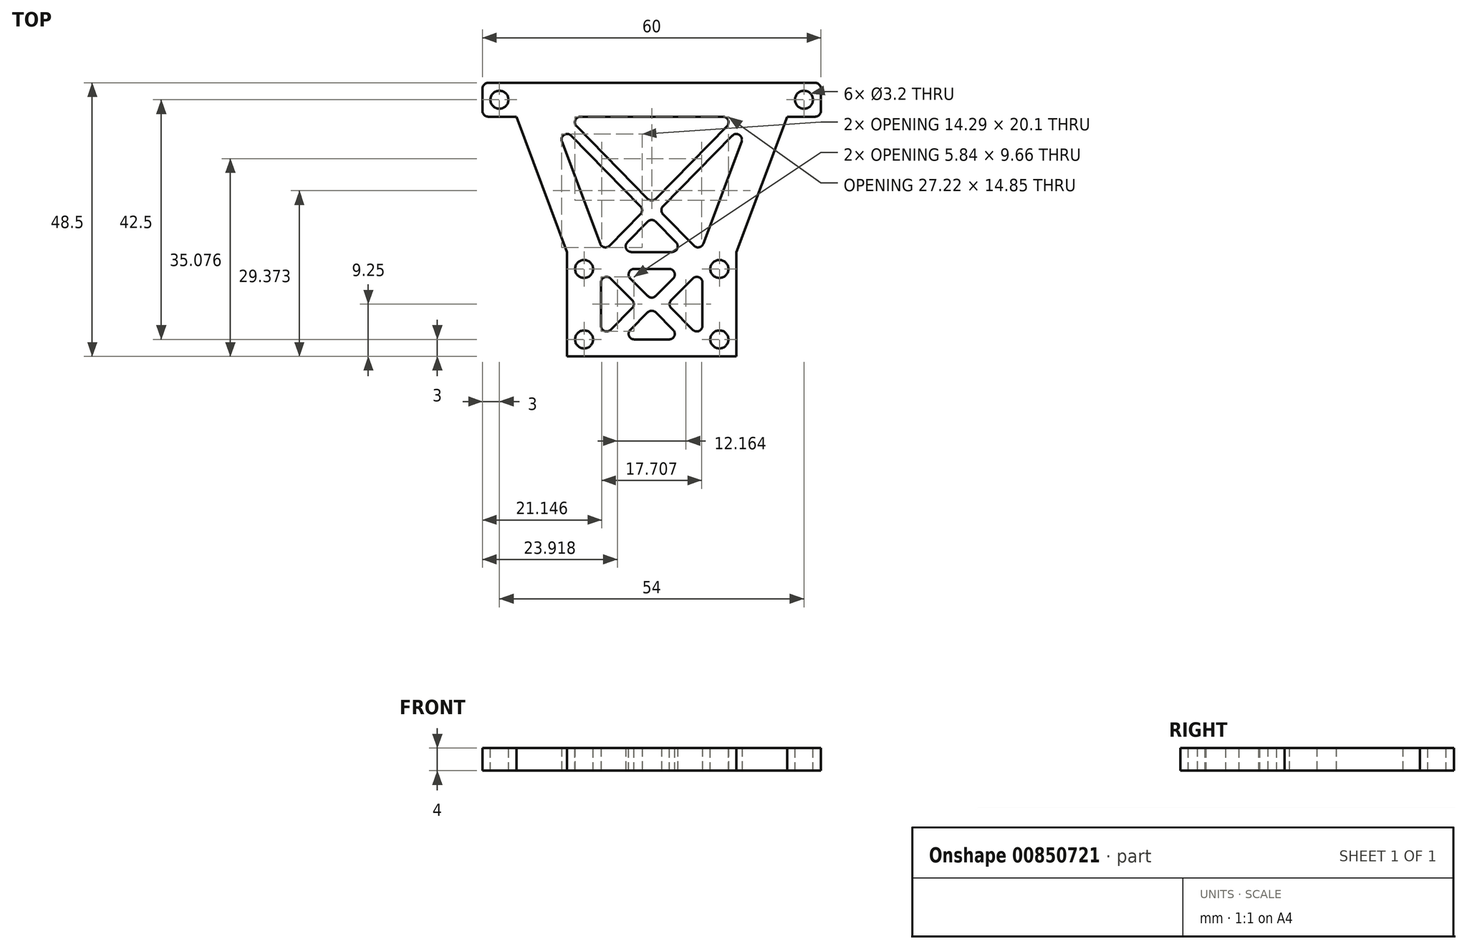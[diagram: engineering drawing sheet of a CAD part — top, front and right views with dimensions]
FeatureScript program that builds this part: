
annotation { "Feature Type Name" : "Feature", "Feature Type Description" : "" }
export const myFeature = defineFeature(function(context is Context, id is Id, definition is map)
    precondition{}
    {
        {
            var Q0;
            Q0=qCreatedBy(makeId("Top.planeOp"),FACE);
            var sketch = newSketch(context, id + "F0", { "sketchPlane" : qUnion([Q0])});
            skLineSegment(sketch, "E0", {"start": v(-15, -9.25) * mm, "end": v(15, -9.25) * mm});
            skLineSegment(sketch, "E1", {"start": v(15, -9.25) * mm, "end": v(15, 9.25) * mm});
            skLineSegment(sketch, "E2", {"start": v(15, 9.25) * mm, "end": v(24, 33.25) * mm});
            skLineSegment(sketch, "E3", {"start": v(24, 33.25) * mm, "end": v(30, 33.25) * mm});
            skLineSegment(sketch, "E4", {"start": v(30, 33.25) * mm, "end": v(30, 39.25) * mm});
            skLineSegment(sketch, "E5", {"start": v(30, 39.25) * mm, "end": v(-30, 39.25) * mm});
            skLineSegment(sketch, "E6", {"start": v(-30, 39.25) * mm, "end": v(-30, 33.25) * mm});
            skLineSegment(sketch, "E7", {"start": v(-30, 33.25) * mm, "end": v(-24, 33.25) * mm});
            skLineSegment(sketch, "E8", {"start": v(-24, 33.25) * mm, "end": v(-15, 9.25) * mm});
            skLineSegment(sketch, "E9", {"start": v(-15, 9.25) * mm, "end": v(-15, -9.25) * mm});
            skLineSegment(sketch, "E10", {"start": v(-15, 9.25) * mm, "end": v(15, 9.25) * mm, "construction": true});
            skSolve(sketch);
        }
        {
            var Q0;
            Q0 = qSketchRegion(id + "F0", true);
            extrude(context, id + "F1", {"entities" : qUnion([Q0]), "depth" : 4 * mm, "offsetDistance" : 25 * mm});
        }
        {
            var Q0;
            Q0=makeQuery(id+"F1.opExtrude","CAP_FACE",FACE,{"disambiguationData":[OSD([sQuery(id+"F0.wireOp",EDGE,"E0"),sQuery(id+"F0.wireOp",EDGE,"E1"),sQuery(id+"F0.wireOp",EDGE,"E2"),sQuery(id+"F0.wireOp",EDGE,"E3"),sQuery(id+"F0.wireOp",EDGE,"E4"),sQuery(id+"F0.wireOp",EDGE,"E5"),sQuery(id+"F0.wireOp",EDGE,"E6"),sQuery(id+"F0.wireOp",EDGE,"E7"),sQuery(id+"F0.wireOp",EDGE,"E8"),sQuery(id+"F0.wireOp",EDGE,"E9")])],"isStart":false});
            var sketch = newSketch(context, id + "F2", { "sketchPlane" : qUnion([Q0])});
            skLineSegment(sketch, "E11.bottom", {"start": v(-12, -6.25) * mm, "end": v(12, -6.25) * mm, "construction": true});
            skLineSegment(sketch, "E11.top", {"start": v(-12, 6.25) * mm, "end": v(12, 6.25) * mm, "construction": true});
            skLineSegment(sketch, "E11.left", {"start": v(-12, -6.25) * mm, "end": v(-12, 6.25) * mm, "construction": true});
            skLineSegment(sketch, "E11.right", {"start": v(12, -6.25) * mm, "end": v(12, 6.25) * mm, "construction": true});
            skLineSegment(sketch, "E12", {"start": v(-15, 9.25) * mm, "end": v(15, 9.25) * mm, "construction": true});
            skLineSegment(sketch, "E13", {"start": v(-12, -6.25) * mm, "end": v(-15, -6.25) * mm, "construction": true});
            skLineSegment(sketch, "E14", {"start": v(-12, -6.25) * mm, "end": v(-12, -9.25) * mm, "construction": true});
            skLineSegment(sketch, "E15", {"start": v(12, 6.25) * mm, "end": v(12, 9.25) * mm, "construction": true});
            skLineSegment(sketch, "E16", {"start": v(12, 6.25) * mm, "end": v(15, 6.25) * mm, "construction": true});
            skCircle(sketch, "E17", {"center": v(-12, 6.25) * mm, "radius": 1.6 * mm});
            skCircle(sketch, "E18", {"center": v(12, 6.25) * mm, "radius": 1.6 * mm});
            skCircle(sketch, "E19", {"center": v(-12, -6.25) * mm, "radius": 1.6 * mm});
            skCircle(sketch, "E20", {"center": v(12, -6.25) * mm, "radius": 1.6 * mm});
            skLineSegment(sketch, "E21", {"start": v(-24, 33.25) * mm, "end": v(-30, 39.25) * mm, "construction": true});
            skLineSegment(sketch, "E22", {"start": v(24, 33.25) * mm, "end": v(30, 39.25) * mm, "construction": true});
            skCircle(sketch, "E23", {"center": v(27, 36.25) * mm, "radius": 1.6 * mm});
            skCircle(sketch, "E24", {"center": v(-27, 36.25) * mm, "radius": 1.6 * mm});
            skSolve(sketch);
        }
        {
            var Q0;
            Q0 = qSketchRegion(id + "F2", true);
            extrude(context, id + "F3", {"entities" : qUnion([Q0]), "operationType" : NewBodyOperationType.REMOVE, "endBound" : BoundingType.UP_TO_NEXT, "oppositeDirection" : true, "depth" : 25 * mm, "offsetDistance" : 25 * mm});
        }
        {
            var Q0;
            Q0=makeQuery(id+"F1.opExtrude","CAP_FACE",FACE,{"disambiguationData":[OSD([sQuery(id+"F0.wireOp",EDGE,"E0"),sQuery(id+"F0.wireOp",EDGE,"E1"),sQuery(id+"F0.wireOp",EDGE,"E2"),sQuery(id+"F0.wireOp",EDGE,"E3"),sQuery(id+"F0.wireOp",EDGE,"E4"),sQuery(id+"F0.wireOp",EDGE,"E5"),sQuery(id+"F0.wireOp",EDGE,"E6"),sQuery(id+"F0.wireOp",EDGE,"E7"),sQuery(id+"F0.wireOp",EDGE,"E8"),sQuery(id+"F0.wireOp",EDGE,"E9")])],"isStart":false});
            var sketch = newSketch(context, id + "F4", { "sketchPlane" : qUnion([Q0])});
            skLineSegment(sketch, "E25", {"start": v(-17.6, 33.25) * mm, "end": v(-8.6, 9.25) * mm});
            skLineSegment(sketch, "E26", {"start": v(-8.6, 9.25) * mm, "end": v(-1.3, 16.67) * mm});
            skLineSegment(sketch, "E27", {"start": v(-1.3, 16.67) * mm, "end": v(-17.6, 33.25) * mm});
            skLineSegment(sketch, "E28", {"start": v(17.6, 33.25) * mm, "end": v(8.6, 9.25) * mm});
            skLineSegment(sketch, "E29", {"start": v(8.6, 9.25) * mm, "end": v(1.3, 16.67) * mm});
            skLineSegment(sketch, "E30", {"start": v(1.3, 16.67) * mm, "end": v(17.6, 33.25) * mm});
            skLineSegment(sketch, "E31", {"start": v(-15, 33.25) * mm, "end": v(15, 33.25) * mm});
            skLineSegment(sketch, "E32", {"start": v(15, 33.25) * mm, "end": v(0, 17.98) * mm});
            skLineSegment(sketch, "E33", {"start": v(0, 17.98) * mm, "end": v(-15, 33.25) * mm});
            skLineSegment(sketch, "E34", {"start": v(-6, 9.25) * mm, "end": v(6, 9.25) * mm});
            skLineSegment(sketch, "E35", {"start": v(6, 9.25) * mm, "end": v(0, 15.36) * mm});
            skLineSegment(sketch, "E36", {"start": v(0, 15.36) * mm, "end": v(-6, 9.25) * mm});
            skLineSegment(sketch, "E37", {"start": v(-24, 33.25) * mm, "end": v(24, 33.25) * mm, "construction": true});
            skLineSegment(sketch, "E38", {"start": v(-15, 9.25) * mm, "end": v(15, 9.25) * mm, "construction": true});
            skLineSegment(sketch, "E39", {"start": v(-1.3, 16.67) * mm, "end": v(0, 15.36) * mm, "construction": true});
            skLineSegment(sketch, "E40", {"start": v(0, 15.36) * mm, "end": v(1.3, 16.67) * mm, "construction": true});
            skLineSegment(sketch, "E41", {"start": v(1.3, 16.67) * mm, "end": v(0, 17.98) * mm, "construction": true});
            skLineSegment(sketch, "E42", {"start": v(0, 17.98) * mm, "end": v(-1.3, 16.67) * mm, "construction": true});
            skLineSegment(sketch, "E43", {"start": v(-12.62, 19.99) * mm, "end": v(-18.24, 17.88) * mm, "construction": true});
            skSolve(sketch);
        }
        {
            var Q0;
            Q0 = qSketchRegion(id + "F4", true);
            extrude(context, id + "F5", {"entities" : qUnion([Q0]), "operationType" : NewBodyOperationType.REMOVE, "endBound" : BoundingType.UP_TO_NEXT, "oppositeDirection" : true, "depth" : 25 * mm, "offsetDistance" : 25 * mm});
        }
        {
            var Q0;
            Q0=makeQuery(id+"F5.boolean.opBoolean","COPY",EDGE,{"derivedFrom":makeQuery(id+"F5.opExtrude","SWEPT_EDGE",EDGE,{"disambiguationData":[OSD([sQuery(id+"F4.wireOp",EDGE,"E28"),sQuery(id+"F4.wireOp",EDGE,"E30")])]})});
            var Q1;
            Q1=makeQuery(id+"F5.boolean.opBoolean","COPY",EDGE,{"derivedFrom":makeQuery(id+"F5.opExtrude","SWEPT_EDGE",EDGE,{"disambiguationData":[OSD([sQuery(id+"F4.wireOp",EDGE,"E31"),sQuery(id+"F4.wireOp",EDGE,"E32")])]})});
            var Q2;
            Q2=makeQuery(id+"F5.boolean.opBoolean","COPY",EDGE,{"derivedFrom":makeQuery(id+"F5.opExtrude","SWEPT_EDGE",EDGE,{"disambiguationData":[OSD([sQuery(id+"F4.wireOp",EDGE,"E31"),sQuery(id+"F4.wireOp",EDGE,"E33")])]})});
            var Q3;
            Q3=makeQuery(id+"F5.boolean.opBoolean","COPY",EDGE,{"derivedFrom":makeQuery(id+"F5.opExtrude","SWEPT_EDGE",EDGE,{"disambiguationData":[OSD([sQuery(id+"F4.wireOp",EDGE,"E25"),sQuery(id+"F4.wireOp",EDGE,"E27")])]})});
            var Q4;
            Q4=makeQuery(id+"F5.boolean.opBoolean","COPY",EDGE,{"derivedFrom":makeQuery(id+"F5.opExtrude","SWEPT_EDGE",EDGE,{"disambiguationData":[OSD([sQuery(id+"F4.wireOp",EDGE,"E32"),sQuery(id+"F4.wireOp",EDGE,"E33")])]})});
            var Q5;
            Q5=makeQuery(id+"F5.boolean.opBoolean","COPY",EDGE,{"derivedFrom":makeQuery(id+"F5.opExtrude","SWEPT_EDGE",EDGE,{"disambiguationData":[OSD([sQuery(id+"F4.wireOp",EDGE,"E28"),sQuery(id+"F4.wireOp",EDGE,"E29")])]})});
            var Q6;
            Q6=makeQuery(id+"F5.boolean.opBoolean","COPY",EDGE,{"derivedFrom":makeQuery(id+"F5.opExtrude","SWEPT_EDGE",EDGE,{"disambiguationData":[OSD([sQuery(id+"F4.wireOp",EDGE,"E25"),sQuery(id+"F4.wireOp",EDGE,"E26")])]})});
            var Q7;
            Q7=makeQuery(id+"F5.boolean.opBoolean","COPY",EDGE,{"derivedFrom":makeQuery(id+"F5.opExtrude","SWEPT_EDGE",EDGE,{"disambiguationData":[OSD([sQuery(id+"F4.wireOp",EDGE,"E34"),sQuery(id+"F4.wireOp",EDGE,"E36")])]})});
            var Q8;
            Q8=makeQuery(id+"F5.boolean.opBoolean","COPY",EDGE,{"derivedFrom":makeQuery(id+"F5.opExtrude","SWEPT_EDGE",EDGE,{"disambiguationData":[OSD([sQuery(id+"F4.wireOp",EDGE,"E34"),sQuery(id+"F4.wireOp",EDGE,"E35")])]})});
            var Q9;
            Q9=makeQuery(id+"F5.boolean.opBoolean","COPY",EDGE,{"derivedFrom":makeQuery(id+"F5.opExtrude","SWEPT_EDGE",EDGE,{"disambiguationData":[OSD([sQuery(id+"F4.wireOp",EDGE,"E35"),sQuery(id+"F4.wireOp",EDGE,"E36")])]})});
            var Q10;
            Q10=makeQuery(id+"F5.boolean.opBoolean","COPY",EDGE,{"derivedFrom":makeQuery(id+"F5.opExtrude","SWEPT_EDGE",EDGE,{"disambiguationData":[OSD([sQuery(id+"F4.wireOp",EDGE,"E26"),sQuery(id+"F4.wireOp",EDGE,"E27")])]})});
            var Q11;
            Q11=makeQuery(id+"F5.boolean.opBoolean","COPY",EDGE,{"derivedFrom":makeQuery(id+"F5.opExtrude","SWEPT_EDGE",EDGE,{"disambiguationData":[OSD([sQuery(id+"F4.wireOp",EDGE,"E29"),sQuery(id+"F4.wireOp",EDGE,"E30")])]})});
            fillet(context, id + "F6", {"entities" : qUnion([Q0, Q1, Q2, Q3, Q4, Q5, Q6, Q7, Q8, Q9, Q10, Q11]), "radius" : 1 * mm, "tangentPropagation" : true, "allowEdgeOverflow" : false});
        }
        {
            var Q0;
            Q0=makeQuery(id+"F1.opExtrude","SWEPT_EDGE",EDGE,{"disambiguationData":[OSD([sQuery(id+"F0.wireOp",EDGE,"E4"),sQuery(id+"F0.wireOp",EDGE,"E5")])]});
            var Q1;
            Q1=makeQuery(id+"F1.opExtrude","SWEPT_EDGE",EDGE,{"disambiguationData":[OSD([sQuery(id+"F0.wireOp",EDGE,"E3"),sQuery(id+"F0.wireOp",EDGE,"E4")])]});
            var Q2;
            Q2=makeQuery(id+"F1.opExtrude","SWEPT_EDGE",EDGE,{"disambiguationData":[OSD([sQuery(id+"F0.wireOp",EDGE,"E6"),sQuery(id+"F0.wireOp",EDGE,"E7")])]});
            var Q3;
            Q3=makeQuery(id+"F1.opExtrude","SWEPT_EDGE",EDGE,{"disambiguationData":[OSD([sQuery(id+"F0.wireOp",EDGE,"E5"),sQuery(id+"F0.wireOp",EDGE,"E6")])]});
            fillet(context, id + "F7", {"entities" : qUnion([Q0, Q1, Q2, Q3]), "radius" : 1 * mm, "tangentPropagation" : true, "allowEdgeOverflow" : false});
        }
        {
            var Q0;
            Q0=makeQuery(id+"F1.opExtrude","CAP_FACE",FACE,{"disambiguationData":[OSD([sQuery(id+"F0.wireOp",EDGE,"E0"),sQuery(id+"F0.wireOp",EDGE,"E1"),sQuery(id+"F0.wireOp",EDGE,"E2"),sQuery(id+"F0.wireOp",EDGE,"E3"),sQuery(id+"F0.wireOp",EDGE,"E4"),sQuery(id+"F0.wireOp",EDGE,"E5"),sQuery(id+"F0.wireOp",EDGE,"E6"),sQuery(id+"F0.wireOp",EDGE,"E7"),sQuery(id+"F0.wireOp",EDGE,"E8"),sQuery(id+"F0.wireOp",EDGE,"E9")])],"isStart":true});
            var sketch = newSketch(context, id + "F8", { "sketchPlane" : qUnion([Q0])});
            skLineSegment(sketch, "E44", {"start": v(-9, -6.25) * mm, "end": v(-9, 6.25) * mm});
            skLineSegment(sketch, "E45", {"start": v(-9, 6.25) * mm, "end": v(-2.75, 0) * mm});
            skLineSegment(sketch, "E46", {"start": v(-2.75, 0) * mm, "end": v(-9, -6.25) * mm});
            skLineSegment(sketch, "E47", {"start": v(-5.5, -6.25) * mm, "end": v(5.5, -6.25) * mm});
            skLineSegment(sketch, "E48", {"start": v(5.5, -6.25) * mm, "end": v(0, -0.74) * mm});
            skLineSegment(sketch, "E49", {"start": v(0, -0.74) * mm, "end": v(-5.5, -6.25) * mm});
            skLineSegment(sketch, "E50", {"start": v(9, -6.25) * mm, "end": v(2.75, 0) * mm});
            skLineSegment(sketch, "E51", {"start": v(2.75, 0) * mm, "end": v(9, 6.25) * mm});
            skLineSegment(sketch, "E52", {"start": v(9, 6.25) * mm, "end": v(9, -6.25) * mm});
            skLineSegment(sketch, "E53", {"start": v(-5.5, 6.25) * mm, "end": v(5.5, 6.25) * mm});
            skLineSegment(sketch, "E54", {"start": v(5.5, 6.25) * mm, "end": v(0, 0.74) * mm});
            skLineSegment(sketch, "E55", {"start": v(0, 0.74) * mm, "end": v(-5.5, 6.25) * mm});
            skLineSegment(sketch, "E56", {"start": v(-9, 6.25) * mm, "end": v(9, 6.25) * mm, "construction": true});
            skLineSegment(sketch, "E57", {"start": v(-9, -6.25) * mm, "end": v(9, -6.25) * mm, "construction": true});
            skSolve(sketch);
        }
        {
            var Q0;
            Q0 = qSketchRegion(id + "F8", true);
            extrude(context, id + "F9", {"entities" : qUnion([Q0]), "operationType" : NewBodyOperationType.REMOVE, "endBound" : BoundingType.UP_TO_NEXT, "oppositeDirection" : true, "depth" : 25 * mm, "offsetDistance" : 25 * mm});
        }
        {
            var Q0;
            Q0=makeQuery(id+"F9.boolean.opBoolean","COPY",EDGE,{"derivedFrom":makeQuery(id+"F9.opExtrude","SWEPT_EDGE",EDGE,{"disambiguationData":[OSD([sQuery(id+"F8.wireOp",EDGE,"E44"),sQuery(id+"F8.wireOp",EDGE,"E46")])]})});
            var Q1;
            Q1=makeQuery(id+"F9.boolean.opBoolean","COPY",EDGE,{"derivedFrom":makeQuery(id+"F9.opExtrude","SWEPT_EDGE",EDGE,{"disambiguationData":[OSD([sQuery(id+"F8.wireOp",EDGE,"E47"),sQuery(id+"F8.wireOp",EDGE,"E49")])]})});
            var Q2;
            Q2=makeQuery(id+"F9.boolean.opBoolean","COPY",EDGE,{"derivedFrom":makeQuery(id+"F9.opExtrude","SWEPT_EDGE",EDGE,{"disambiguationData":[OSD([sQuery(id+"F8.wireOp",EDGE,"E47"),sQuery(id+"F8.wireOp",EDGE,"E48")])]})});
            var Q3;
            Q3=makeQuery(id+"F9.boolean.opBoolean","COPY",EDGE,{"derivedFrom":makeQuery(id+"F9.opExtrude","SWEPT_EDGE",EDGE,{"disambiguationData":[OSD([sQuery(id+"F8.wireOp",EDGE,"E50"),sQuery(id+"F8.wireOp",EDGE,"E52")])]})});
            var Q4;
            Q4=makeQuery(id+"F9.boolean.opBoolean","COPY",EDGE,{"derivedFrom":makeQuery(id+"F9.opExtrude","SWEPT_EDGE",EDGE,{"disambiguationData":[OSD([sQuery(id+"F8.wireOp",EDGE,"E44"),sQuery(id+"F8.wireOp",EDGE,"E45")])]})});
            var Q5;
            Q5=makeQuery(id+"F9.boolean.opBoolean","COPY",EDGE,{"derivedFrom":makeQuery(id+"F9.opExtrude","SWEPT_EDGE",EDGE,{"disambiguationData":[OSD([sQuery(id+"F8.wireOp",EDGE,"E45"),sQuery(id+"F8.wireOp",EDGE,"E46")])]})});
            var Q6;
            Q6=makeQuery(id+"F9.boolean.opBoolean","COPY",EDGE,{"derivedFrom":makeQuery(id+"F9.opExtrude","SWEPT_EDGE",EDGE,{"disambiguationData":[OSD([sQuery(id+"F8.wireOp",EDGE,"E53"),sQuery(id+"F8.wireOp",EDGE,"E54")])]})});
            var Q7;
            Q7=makeQuery(id+"F9.boolean.opBoolean","COPY",EDGE,{"derivedFrom":makeQuery(id+"F9.opExtrude","SWEPT_EDGE",EDGE,{"disambiguationData":[OSD([sQuery(id+"F8.wireOp",EDGE,"E51"),sQuery(id+"F8.wireOp",EDGE,"E52")])]})});
            var Q8;
            Q8=makeQuery(id+"F9.boolean.opBoolean","COPY",EDGE,{"derivedFrom":makeQuery(id+"F9.opExtrude","SWEPT_EDGE",EDGE,{"disambiguationData":[OSD([sQuery(id+"F8.wireOp",EDGE,"E50"),sQuery(id+"F8.wireOp",EDGE,"E51")])]})});
            var Q9;
            Q9=makeQuery(id+"F9.boolean.opBoolean","COPY",EDGE,{"derivedFrom":makeQuery(id+"F9.opExtrude","SWEPT_EDGE",EDGE,{"disambiguationData":[OSD([sQuery(id+"F8.wireOp",EDGE,"E54"),sQuery(id+"F8.wireOp",EDGE,"E55")])]})});
            var Q10;
            Q10=makeQuery(id+"F9.boolean.opBoolean","COPY",EDGE,{"derivedFrom":makeQuery(id+"F9.opExtrude","SWEPT_EDGE",EDGE,{"disambiguationData":[OSD([sQuery(id+"F8.wireOp",EDGE,"E53"),sQuery(id+"F8.wireOp",EDGE,"E55")])]})});
            var Q11;
            Q11=makeQuery(id+"F9.boolean.opBoolean","COPY",EDGE,{"derivedFrom":makeQuery(id+"F9.opExtrude","SWEPT_EDGE",EDGE,{"disambiguationData":[OSD([sQuery(id+"F8.wireOp",EDGE,"E48"),sQuery(id+"F8.wireOp",EDGE,"E49")])]})});
            fillet(context, id + "F10", {"entities" : qUnion([Q0, Q1, Q2, Q3, Q4, Q5, Q6, Q7, Q8, Q9, Q10, Q11]), "radius" : 1 * mm, "tangentPropagation" : true, "allowEdgeOverflow" : false});
        }
    });
